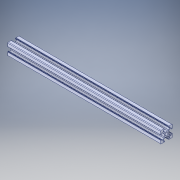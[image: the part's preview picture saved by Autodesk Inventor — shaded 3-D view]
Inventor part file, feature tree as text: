
AUTODESK INVENTOR PART (.ipt)
format: ipt  version: 2018 (Build 220112000, 112)  size: 371,200 bytes
history: native  units: in
note: dims shown in document units (in); Inventor stores cm internally (conversion verified against a paired STEP export)
features: extrude x1, sketch x1, projected_geometry x1, fillet x1
ambient origin geometry x8: Origin, YZ Plane, XZ Plane, XY Plane, X Axis, Y Axis, Z Axis, Center Point
bodies: Solid1 (feature_tree)
feature tree (4):
  extrude  "Extrusion2"  [1 undecoded]
  sketch  "Sketch3"  dims[d2=6.2992in d3=0.0in]
  projected_geometry  "Projected Loop2"
  fillet  "Fillet5"  [1 undecoded]
note: 2 required parameter values undecoded (feature->parameter linkage not recoverable at this tier; creation-order binding heuristic only, values carry confidence <= 0.55)
